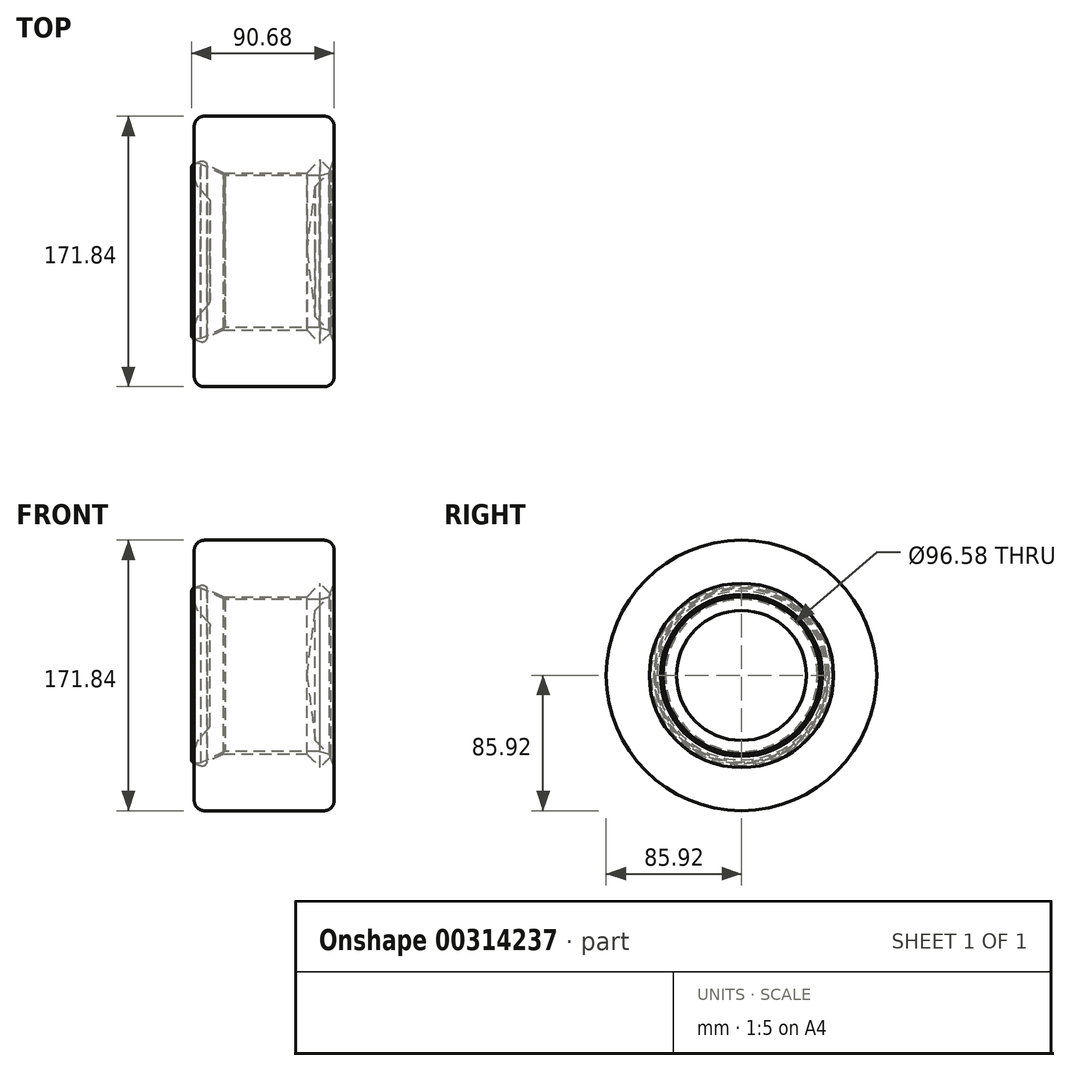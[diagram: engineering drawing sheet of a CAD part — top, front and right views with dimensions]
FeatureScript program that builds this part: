
annotation { "Feature Type Name" : "Feature", "Feature Type Description" : "" }
export const myFeature = defineFeature(function(context is Context, id is Id, definition is map)
    precondition{}
    {
        {
            var Q0;
            Q0=qCreatedBy(makeId("Top.planeOp"),FACE);
            var sketch = newSketch(context, id + "F0", { "sketchPlane" : qUnion([Q0])});
            skLineSegment(sketch, "E0", {"start": v(-20.08, 0) * mm, "end": v(-20.08, 31.2) * mm});
            skLineSegment(sketch, "E1", {"start": v(-20.9, 33.33) * mm, "end": v(-27.7, 40.85) * mm});
            skLineSegment(sketch, "E2", {"start": v(-28.33, 41.9) * mm, "end": v(-31.91, 51.81) * mm});
            skLineSegment(sketch, "E3", {"start": v(-30, 55.88) * mm, "end": v(-26.2, 57.25) * mm});
            skLineSegment(sketch, "E4", {"start": v(-22.14, 55.35) * mm, "end": v(-21.94, 54.8) * mm});
            skLineSegment(sketch, "E5", {"start": v(-21.94, 54.8) * mm, "end": v(-11.76, 49.92) * mm});
            skLineSegment(sketch, "E6", {"start": v(-11.76, 49.92) * mm, "end": v(41.31, 49.92) * mm});
            skLineSegment(sketch, "E7", {"start": v(41.31, 49.92) * mm, "end": v(49.63, 58.33) * mm});
            skLineSegment(sketch, "E8", {"start": v(49.63, 58.33) * mm, "end": v(56.6, 51.43) * mm});
            skLineSegment(sketch, "E9", {"start": v(56.6, 51.43) * mm, "end": v(46.6, 41.31) * mm});
            skLineSegment(sketch, "E10", {"start": v(46.6, 41.31) * mm, "end": v(41.31, 0) * mm});
            skLineSegment(sketch, "E11", {"start": v(41.31, 0) * mm, "end": v(-20.08, 0) * mm});
            skPoint(sketch, "E12.visualSharp", {"position": v(-33, 54.8) * mm});
            skArc(sketch, "E12.filletArc", {"start": v(-30, 55.88) * mm, "mid": v(-31.8, 54.24) * mm, "end": v(-31.91, 51.81) * mm});
            skPoint(sketch, "E13.visualSharp", {"position": v(-23.22, 58.33) * mm});
            skArc(sketch, "E13.filletArc", {"start": v(-22.14, 55.35) * mm, "mid": v(-23.78, 57.14) * mm, "end": v(-26.2, 57.25) * mm});
            skPoint(sketch, "E14.visualSharp", {"position": v(-28.12, 41.31) * mm});
            skArc(sketch, "E14.filletArc", {"start": v(-28.33, 41.9) * mm, "mid": v(-28.06, 41.34) * mm, "end": v(-27.7, 40.85) * mm});
            skPoint(sketch, "E15.visualSharp", {"position": v(-20.08, 32.42) * mm});
            skArc(sketch, "E15.filletArc", {"start": v(-20.08, 31.2) * mm, "mid": v(-20.3, 32.34) * mm, "end": v(-20.9, 33.33) * mm});
            skSolve(sketch);
        }
        {
            var Q0;
            Q0 = qSketchRegion(id + "F0", true);
            var Q1;
            Q1=sQuery(id+"F0.wireOp",EDGE,"E11");
            revolve(context, id + "F1", {"entities" : qUnion([Q0]), "axis" : qUnion([Q1]), "revolveType" : RevolveType.FULL});
        }
        {
            var Q0;
            Q0=makeQuery(id+"F0.imprint","IMPRINT",FACE,{"disambiguationData":[TD([[makeQuery(id+"F0.imprint","IMPRINT",EDGE,{"derivedFrom":sQuery(id+"F0.wireOp",EDGE,"E0")}),-1.0]])]});
            var Q1;
            Q1=sQuery(id+"F0.wireOp",EDGE,"E11");
            revolve(context, id + "F2", {"entities" : qUnion([Q0]), "axis" : qUnion([Q1]), "revolveType" : RevolveType.FULL});
        }
        {
            var Q0;
            Q0=qCreatedBy(makeId("Top.planeOp"),FACE);
            var sketch = newSketch(context, id + "F3", { "sketchPlane" : qUnion([Q0])});
            skLineSegment(sketch, "E16", {"start": v(-30.21, 55.8) * mm, "end": v(-30.21, 79.57) * mm});
            skLineSegment(sketch, "E17", {"start": v(-23.86, 85.92) * mm, "end": v(52.23, 85.92) * mm});
            skLineSegment(sketch, "E18", {"start": v(58.58, 79.57) * mm, "end": v(58.58, 58.55) * mm});
            skLineSegment(sketch, "E19", {"start": v(49.35, 48.29) * mm, "end": v(-10.73, 48.29) * mm});
            skLineSegment(sketch, "E20", {"start": v(-10.73, 48.29) * mm, "end": v(-22, 53.64) * mm});
            skLineSegment(sketch, "E21", {"start": v(-22, 53.64) * mm, "end": v(-26.17, 55.4) * mm});
            skLineSegment(sketch, "E22", {"start": v(-26.17, 55.4) * mm, "end": v(-30.21, 55.8) * mm});
            skPoint(sketch, "E23.visualSharp", {"position": v(-30.21, 85.92) * mm});
            skArc(sketch, "E23.filletArc", {"start": v(-23.86, 85.92) * mm, "mid": v(-28.36, 84.06) * mm, "end": v(-30.21, 79.57) * mm});
            skPoint(sketch, "E24.visualSharp", {"position": v(58.58, 85.92) * mm});
            skArc(sketch, "E24.filletArc", {"start": v(58.58, 79.57) * mm, "mid": v(56.72, 84.06) * mm, "end": v(52.23, 85.92) * mm});
            skLineSegment(sketch, "E25", {"start": v(58.58, 58.55) * mm, "end": v(55.3, 49.9) * mm});
            skLineSegment(sketch, "E26", {"start": v(55.3, 49.9) * mm, "end": v(49.35, 48.29) * mm});
            skLineSegment(sketch, "E27", {"start": v(-34.94, 0) * mm, "end": v(66.2, 0) * mm});
            skSolve(sketch);
        }
        {
            var Q0;
            Q0 = qSketchRegion(id + "F3", true);
            var Q1;
            Q1=sQuery(id+"F3.wireOp",EDGE,"E27");
            revolve(context, id + "F4", {"entities" : qUnion([Q0]), "axis" : qUnion([Q1]), "revolveType" : RevolveType.FULL});
        }
    });
